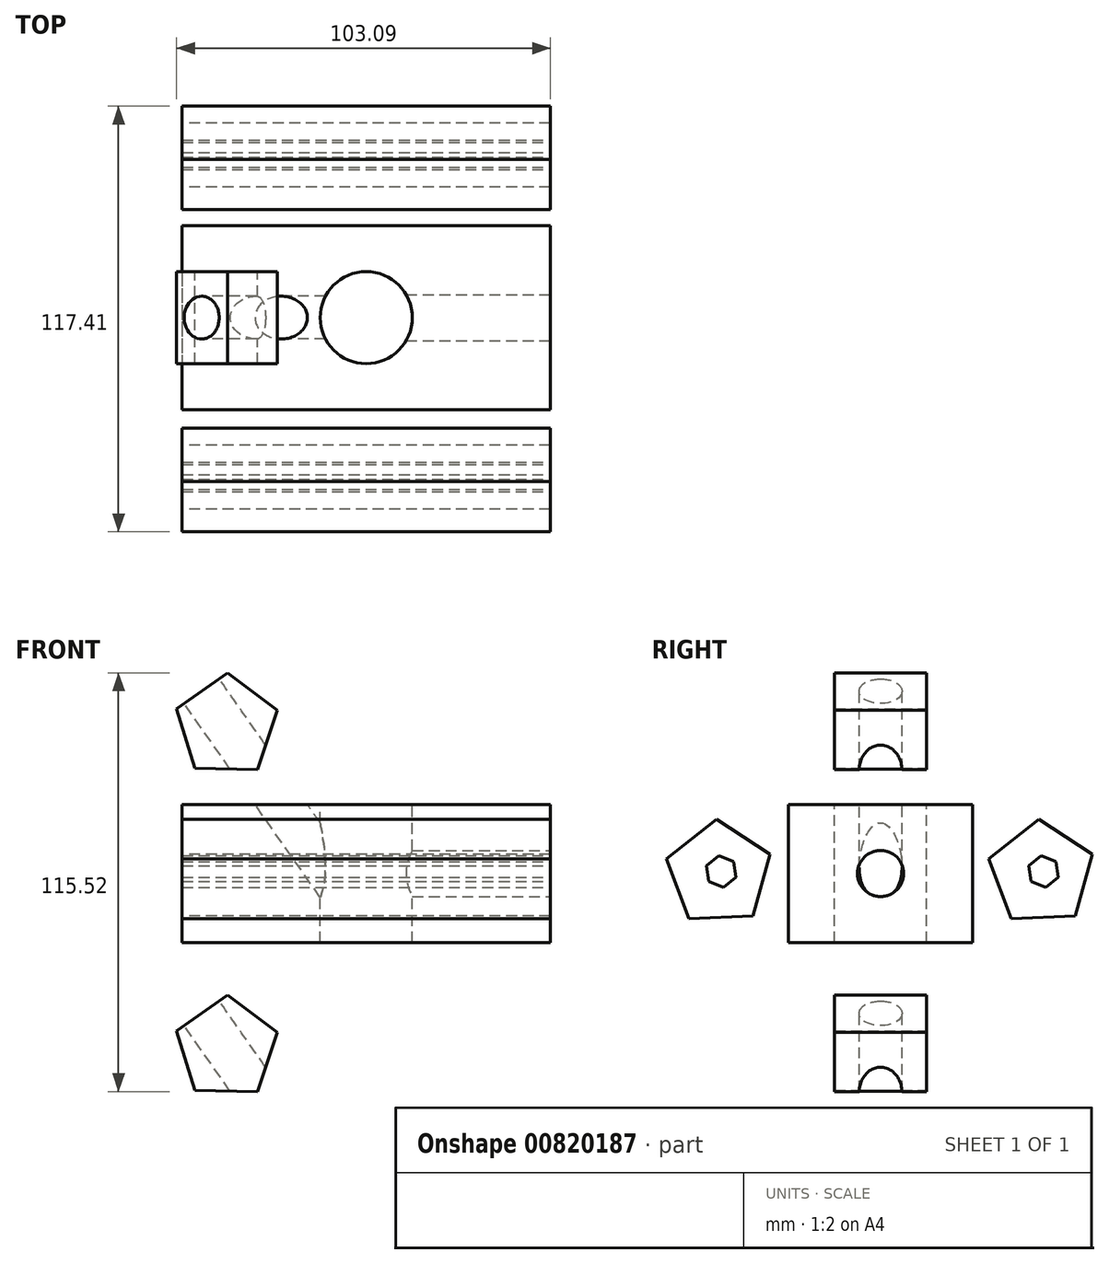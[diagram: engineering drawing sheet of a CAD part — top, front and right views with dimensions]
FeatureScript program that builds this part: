
annotation { "Feature Type Name" : "Feature", "Feature Type Description" : "" }
export const myFeature = defineFeature(function(context is Context, id is Id, definition is map)
    precondition{}
    {
        {
            var Q0;
            Q0=qCreatedBy(makeId("Top.planeOp"),FACE);
            var sketch = newSketch(context, id + "F0", { "sketchPlane" : qUnion([Q0])});
            skLineSegment(sketch, "E0.bottom", {"start": v(-50.8, 25.4) * mm, "end": v(50.8, 25.4) * mm});
            skLineSegment(sketch, "E0.top", {"start": v(-50.8, -25.4) * mm, "end": v(50.8, -25.4) * mm});
            skLineSegment(sketch, "E0.left", {"start": v(-50.8, 25.4) * mm, "end": v(-50.8, -25.4) * mm});
            skLineSegment(sketch, "E0.right", {"start": v(50.8, 25.4) * mm, "end": v(50.8, -25.4) * mm});
            skSolve(sketch);
        }
        {
            var Q0;
            Q0=makeQuery(id+"F0.imprint","IMPRINT",FACE,{"disambiguationData":[TD([[makeQuery(id+"F0.imprint","IMPRINT",EDGE,{"derivedFrom":sQuery(id+"F0.wireOp",EDGE,"E0.bottom")}),-1.0]])]});
            extrude(context, id + "F1", {"entities" : qUnion([Q0]), "endBound" : BoundingType.SYMMETRIC, "depth" : 38.1 * mm, "offsetDistance" : 25.4 * mm});
        }
        {
            var Q0;
            Q0=makeQuery(id+"F1.opExtrude","CAP_FACE",FACE,{"disambiguationData":[OSD([sQuery(id+"F0.wireOp",EDGE,"E0.bottom"),sQuery(id+"F0.wireOp",EDGE,"E0.top"),sQuery(id+"F0.wireOp",EDGE,"E0.left"),sQuery(id+"F0.wireOp",EDGE,"E0.right")])],"isStart":false});
            var sketch = newSketch(context, id + "F2", { "sketchPlane" : qUnion([Q0])});
            skCircle(sketch, "E1", {"center": v(0, 0) * mm, "radius": 12.7 * mm});
            skSolve(sketch);
        }
        {
            var Q0;
            Q0=makeQuery(id+"F2.imprint","IMPRINT",FACE,{"disambiguationData":[TD([[makeQuery(id+"F2.imprint","IMPRINT",EDGE,{"derivedFrom":sQuery(id+"F2.wireOp",EDGE,"E1")}),1.0]])]});
            extrude(context, id + "F3", {"entities" : qUnion([Q0]), "operationType" : NewBodyOperationType.REMOVE, "endBound" : BoundingType.THROUGH_ALL, "oppositeDirection" : true, "depth" : 25.4 * mm, "offsetDistance" : 25.4 * mm});
        }
        {
            var Q0;
            Q0=makeQuery(id+"F1.opExtrude","SWEPT_FACE",FACE,{"disambiguationData":[OSD([sQuery(id+"F0.wireOp",EDGE,"E0.right")])]});
            var sketch = newSketch(context, id + "F4", { "sketchPlane" : qUnion([Q0])});
            skCircle(sketch, "E2", {"center": v(0, 0) * mm, "radius": 6.35 * mm});
            skSolve(sketch);
        }
        {
            var Q0;
            Q0=makeQuery(id+"F4.imprint","IMPRINT",FACE,{"disambiguationData":[TD([[makeQuery(id+"F4.imprint","IMPRINT",EDGE,{"derivedFrom":sQuery(id+"F4.wireOp",EDGE,"E2")}),1.0]])]});
            extrude(context, id + "F5", {"entities" : qUnion([Q0]), "operationType" : NewBodyOperationType.REMOVE, "oppositeDirection" : true, "depth" : 50.8 * mm, "offsetDistance" : 25.4 * mm});
        }
        {
            var Q0;
            Q0=qCreatedBy(makeId("Front.planeOp"),FACE);
            var sketch = newSketch(context, id + "F6", { "sketchPlane" : qUnion([Q0])});
            skCircle(sketch, "E3.cCircle", {"center": v(-38.45, 40.71) * mm, "radius": 11.84 * mm, "construction": true});
            skLineSegment(sketch, "E3.0", {"start": v(-30.04, 28.73) * mm, "end": v(-47.25, 29.01) * mm});
            skLineSegment(sketch, "E3.1", {"start": v(-47.25, 29.01) * mm, "end": v(-52.3, 45.47) * mm});
            skLineSegment(sketch, "E3.2", {"start": v(-52.3, 45.47) * mm, "end": v(-38.2, 55.35) * mm});
            skLineSegment(sketch, "E3.3", {"start": v(-38.2, 55.35) * mm, "end": v(-24.46, 45) * mm});
            skLineSegment(sketch, "E3.4", {"start": v(-24.46, 45) * mm, "end": v(-30.04, 28.73) * mm});
            skPoint(sketch, "E3.0.midPoint", {"position": v(-38.65, 28.87) * mm});
            skSolve(sketch);
        }
        {
            var Q0;
            Q0=makeQuery(id+"F6.imprint","IMPRINT",FACE,{"disambiguationData":[TD([[makeQuery(id+"F6.imprint","IMPRINT",EDGE,{"derivedFrom":sQuery(id+"F6.wireOp",EDGE,"E3.0")}),-1.0]])]});
            extrude(context, id + "F7", {"entities" : qUnion([Q0]), "endBound" : BoundingType.SYMMETRIC, "depth" : 25.4 * mm, "offsetDistance" : 25.4 * mm});
        }
        {
            var Q0;
            Q0=makeQuery(id+"F7.opExtrude","SWEPT_FACE",FACE,{"disambiguationData":[OSD([sQuery(id+"F6.wireOp",EDGE,"E3.3")])]});
            var sketch = newSketch(context, id + "F8", { "sketchPlane" : qUnion([Q0])});
            skCircle(sketch, "E4", {"center": v(-54.75, 0) * mm, "radius": 4.52 * mm});
            skSolve(sketch);
        }
        {
            var Q0;
            Q0=sQuery(id+"F8.wireOp",EDGE,"E4");
            extrude(context, id + "F9", {"bodyType" : ToolBodyType.SURFACE, "operationType" : NewBodyOperationType.REMOVE, "surfaceEntities" : qUnion([Q0]), "depth" : 25.4 * mm, "offsetDistance" : 25.4 * mm});
        }
        {
            var Q0;
            Q0=makeQuery(id+"F7.opExtrude","SWEPT_FACE",FACE,{"disambiguationData":[OSD([sQuery(id+"F6.wireOp",EDGE,"E3.2")])]});
            var sketch = newSketch(context, id + "F10", { "sketchPlane" : qUnion([Q0])});
            skCircle(sketch, "E5", {"center": v(-8.26, 0) * mm, "radius": 5.9 * mm});
            skSolve(sketch);
        }
        {
            var Q0;
            Q0=makeQuery(id+"F10.imprint","IMPRINT",FACE,{"disambiguationData":[TD([[makeQuery(id+"F10.imprint","IMPRINT",EDGE,{"derivedFrom":sQuery(id+"F10.wireOp",EDGE,"E5")}),1.0]])]});
            extrude(context, id + "F11", {"entities" : qUnion([Q0]), "operationType" : NewBodyOperationType.REMOVE, "endBound" : BoundingType.THROUGH_ALL, "oppositeDirection" : true, "depth" : 25.4 * mm, "offsetDistance" : 25.4 * mm});
        }
        {
            var Q0;
            Q0=qCreatedBy(makeId("Right.planeOp"),FACE);
            var sketch = newSketch(context, id + "F12", { "sketchPlane" : qUnion([Q0])});
            skCircle(sketch, "E6.cCircle", {"center": v(44.3, 0) * mm, "radius": 12.14 * mm, "construction": true});
            skLineSegment(sketch, "E6.0", {"start": v(58.34, 5.28) * mm, "end": v(53.65, -11.73) * mm});
            skLineSegment(sketch, "E6.1", {"start": v(53.65, -11.73) * mm, "end": v(36.03, -12.53) * mm});
            skLineSegment(sketch, "E6.2", {"start": v(36.03, -12.53) * mm, "end": v(29.83, 3.99) * mm});
            skLineSegment(sketch, "E6.3", {"start": v(29.83, 3.99) * mm, "end": v(43.62, 15) * mm});
            skLineSegment(sketch, "E6.4", {"start": v(43.62, 15) * mm, "end": v(58.34, 5.28) * mm});
            skPoint(sketch, "E6.0.midPoint", {"position": v(56, -3.23) * mm});
            skSolve(sketch);
        }
        {
            var Q0;
            Q0=makeQuery(id+"F12.imprint","IMPRINT",FACE,{"disambiguationData":[TD([[makeQuery(id+"F12.imprint","IMPRINT",EDGE,{"derivedFrom":sQuery(id+"F12.wireOp",EDGE,"E6.0")}),-1.0]])]});
            extrude(context, id + "F13", {"entities" : qUnion([Q0]), "endBound" : BoundingType.SYMMETRIC, "depth" : 101.6 * mm, "offsetDistance" : 25.4 * mm});
        }
        {
            var Q0;
            Q0=makeQuery(id+"F13.opExtrude","CAP_FACE",FACE,{"disambiguationData":[OSD([sQuery(id+"F12.wireOp",EDGE,"E6.0"),sQuery(id+"F12.wireOp",EDGE,"E6.1"),sQuery(id+"F12.wireOp",EDGE,"E6.2"),sQuery(id+"F12.wireOp",EDGE,"E6.3"),sQuery(id+"F12.wireOp",EDGE,"E6.4")])],"isStart":false});
            var sketch = newSketch(context, id + "F14", { "sketchPlane" : qUnion([Q0])});
            skCircle(sketch, "E7.cCircle", {"center": v(44.97, 0.56) * mm, "radius": 3.8 * mm, "construction": true});
            skLineSegment(sketch, "E7.0", {"start": v(41.54, -2.17) * mm, "end": v(40.9, 2.17) * mm});
            skLineSegment(sketch, "E7.1", {"start": v(40.9, 2.17) * mm, "end": v(44.32, 4.9) * mm});
            skLineSegment(sketch, "E7.2", {"start": v(44.32, 4.9) * mm, "end": v(48.4, 3.29) * mm});
            skLineSegment(sketch, "E7.3", {"start": v(48.4, 3.29) * mm, "end": v(49.04, -1.04) * mm});
            skLineSegment(sketch, "E7.4", {"start": v(49.04, -1.04) * mm, "end": v(45.61, -3.77) * mm});
            skLineSegment(sketch, "E7.5", {"start": v(45.61, -3.77) * mm, "end": v(41.54, -2.17) * mm});
            skPoint(sketch, "E7.0.midPoint", {"position": v(41.22, 0) * mm});
            skSolve(sketch);
        }
        {
            var Q0;
            Q0 = qSketchRegion(id + "F14", true);
            extrude(context, id + "F15", {"entities" : qUnion([Q0]), "operationType" : NewBodyOperationType.REMOVE, "endBound" : BoundingType.THROUGH_ALL, "oppositeDirection" : true, "depth" : 25.4 * mm, "offsetDistance" : 25.4 * mm});
        }
        {
            var Q0;
            Q0=makeQuery(id+"F13.opExtrude","SWEPT_BODY",BODY,{"disambiguationData":[OSD([sQuery(id+"F12.wireOp",EDGE,"E6.0"),sQuery(id+"F12.wireOp",EDGE,"E6.1"),sQuery(id+"F12.wireOp",EDGE,"E6.2"),sQuery(id+"F12.wireOp",EDGE,"E6.3"),sQuery(id+"F12.wireOp",EDGE,"E6.4")])]});
            transform(context, id + "F16", {"entities" : qUnion([Q0]), "transformType" : TransformType.TRANSLATION_3D, "dx" : 0 * mm, "dy" : -88.9 * mm, "dz" : 0 * mm, "makeCopy" : true});
        }
        {
            var Q0;
            Q0=makeQuery(id+"F7.opExtrude","SWEPT_BODY",BODY,{"disambiguationData":[OSD([sQuery(id+"F6.wireOp",EDGE,"E3.0"),sQuery(id+"F6.wireOp",EDGE,"E3.1"),sQuery(id+"F6.wireOp",EDGE,"E3.2"),sQuery(id+"F6.wireOp",EDGE,"E3.3"),sQuery(id+"F6.wireOp",EDGE,"E3.4")])]});
            transform(context, id + "F17", {"entities" : qUnion([Q0]), "transformType" : TransformType.TRANSLATION_3D, "dx" : 0 * mm, "dy" : 0 * mm, "dz" : -88.9 * mm, "makeCopy" : true});
        }
    });
